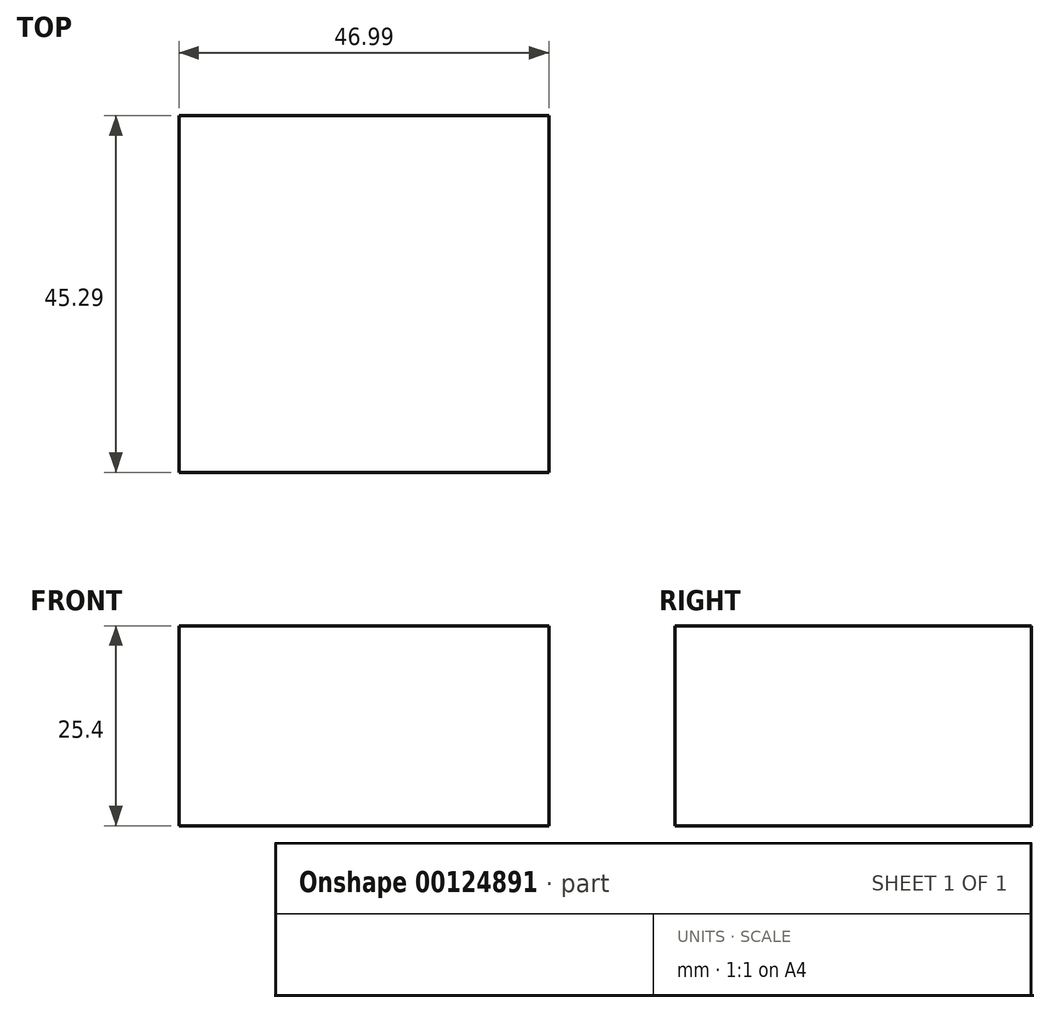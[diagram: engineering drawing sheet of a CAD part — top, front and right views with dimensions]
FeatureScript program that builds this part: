
annotation { "Feature Type Name" : "Feature", "Feature Type Description" : "" }
export const myFeature = defineFeature(function(context is Context, id is Id, definition is map)
    precondition{}
    {
        {
            var Q0;
            Q0=qCreatedBy(makeId("Top.planeOp"),FACE);
            var sketch = newSketch(context, id + "F0", { "sketchPlane" : qUnion([Q0])});
            skLineSegment(sketch, "E0.bottom", {"start": v(-26.8, 17.17) * mm, "end": v(20.2, 17.17) * mm});
            skLineSegment(sketch, "E0.top", {"start": v(-26.8, -28.12) * mm, "end": v(20.2, -28.12) * mm});
            skLineSegment(sketch, "E0.left", {"start": v(-26.8, 17.17) * mm, "end": v(-26.8, -28.12) * mm});
            skLineSegment(sketch, "E0.right", {"start": v(20.2, 17.17) * mm, "end": v(20.2, -28.12) * mm});
            skSolve(sketch);
        }
        {
            var Q0;
            Q0=makeQuery(id+"F0.imprint","IMPRINT",FACE,{"disambiguationData":[TD([[makeQuery(id+"F0.imprint","IMPRINT",EDGE,{"derivedFrom":sQuery(id+"F0.wireOp",EDGE,"E0.bottom")}),-1.0]])]});
            extrude(context, id + "F1", {"entities" : qUnion([Q0]), "depth" : 25.4 * mm});
        }
    });
